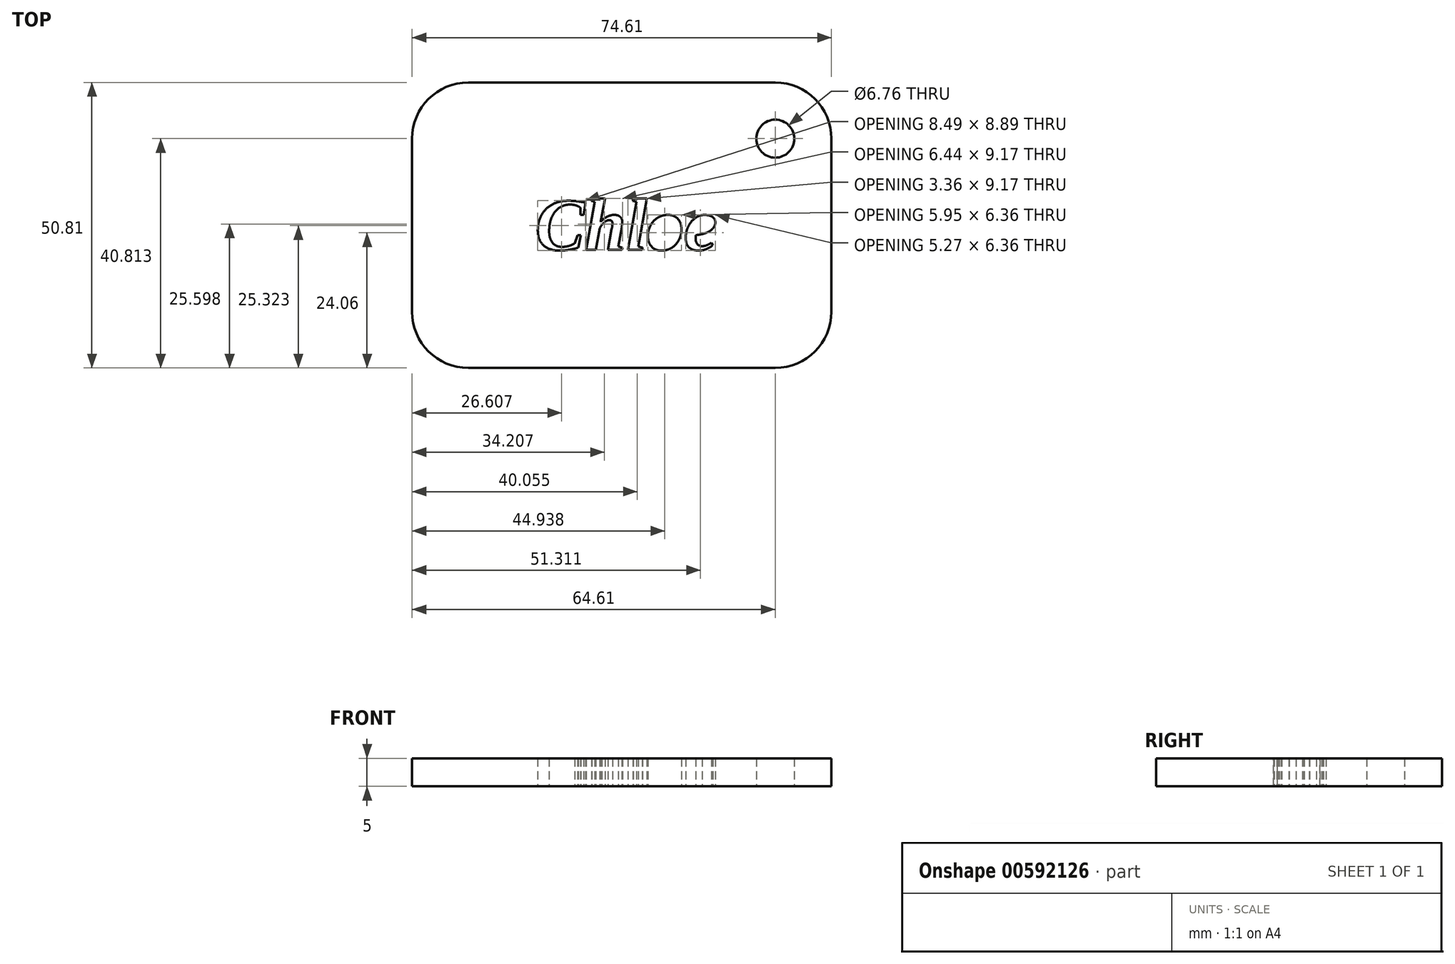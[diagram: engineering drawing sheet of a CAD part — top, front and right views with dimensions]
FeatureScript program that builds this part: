
annotation { "Feature Type Name" : "Feature", "Feature Type Description" : "" }
export const myFeature = defineFeature(function(context is Context, id is Id, definition is map)
    precondition{}
    {
        {
            var Q0;
            Q0=qCreatedBy(makeId("Top.planeOp"),FACE);
            var sketch = newSketch(context, id + "F0", { "sketchPlane" : qUnion([Q0])});
            skLineSegment(sketch, "E0.bottom", {"start": v(-10, 0) * mm, "end": v(-64.61, 0) * mm});
            skLineSegment(sketch, "E0.top", {"start": v(-10, 50.81) * mm, "end": v(-64.61, 50.81) * mm});
            skLineSegment(sketch, "E0.left", {"start": v(0, 10) * mm, "end": v(0, 40.81) * mm});
            skLineSegment(sketch, "E0.right", {"start": v(-74.61, 10) * mm, "end": v(-74.61, 40.81) * mm});
            skPoint(sketch, "E1.visualSharp", {"position": v(-74.61, 50.81) * mm});
            skArc(sketch, "E1.filletArc", {"start": v(-64.61, 50.81) * mm, "mid": v(-71.69, 47.88) * mm, "end": v(-74.61, 40.81) * mm});
            skPoint(sketch, "E2.visualSharp", {"position": v(-74.61, 0) * mm});
            skArc(sketch, "E2.filletArc", {"start": v(-74.61, 10) * mm, "mid": v(-71.69, 2.93) * mm, "end": v(-64.61, 0) * mm});
            skPoint(sketch, "E3.visualSharp", {"position": v(0, 0) * mm});
            skArc(sketch, "E3.filletArc", {"start": v(-10, 0) * mm, "mid": v(-2.93, 2.93) * mm, "end": v(0, 10) * mm});
            skPoint(sketch, "E4.visualSharp", {"position": v(0, 50.81) * mm});
            skArc(sketch, "E4.filletArc", {"start": v(0, 40.81) * mm, "mid": v(-2.93, 47.88) * mm, "end": v(-10, 50.81) * mm});
            skCircle(sketch, "E5", {"center": v(-10, 40.81) * mm, "radius": 3.38 * mm});
            skText(sketch, "E6", { "text": "Chloe", "fontName": "Tinos-BoldItalic.ttf"});
            const initialGuessF0  = {"E6": [-0.0527, 0.02101, 1, 0, 0.00952]};
            skSetInitialGuess(sketch, initialGuessF0);
            skSolve(sketch);
        }
        {
            var Q0;
            Q0=makeQuery(id+"F0.imprint","IMPRINT",FACE,{"disambiguationData":[TD([[makeQuery(id+"F0.imprint","IMPRINT",EDGE,{"derivedFrom":sQuery(id+"F0.wireOp",EDGE,"E0.bottom")}),-1.0]])]});
            extrude(context, id + "F1", {"entities" : qUnion([Q0]), "depth" : 5 * mm, "offsetDistance" : 25 * mm});
        }
    });
